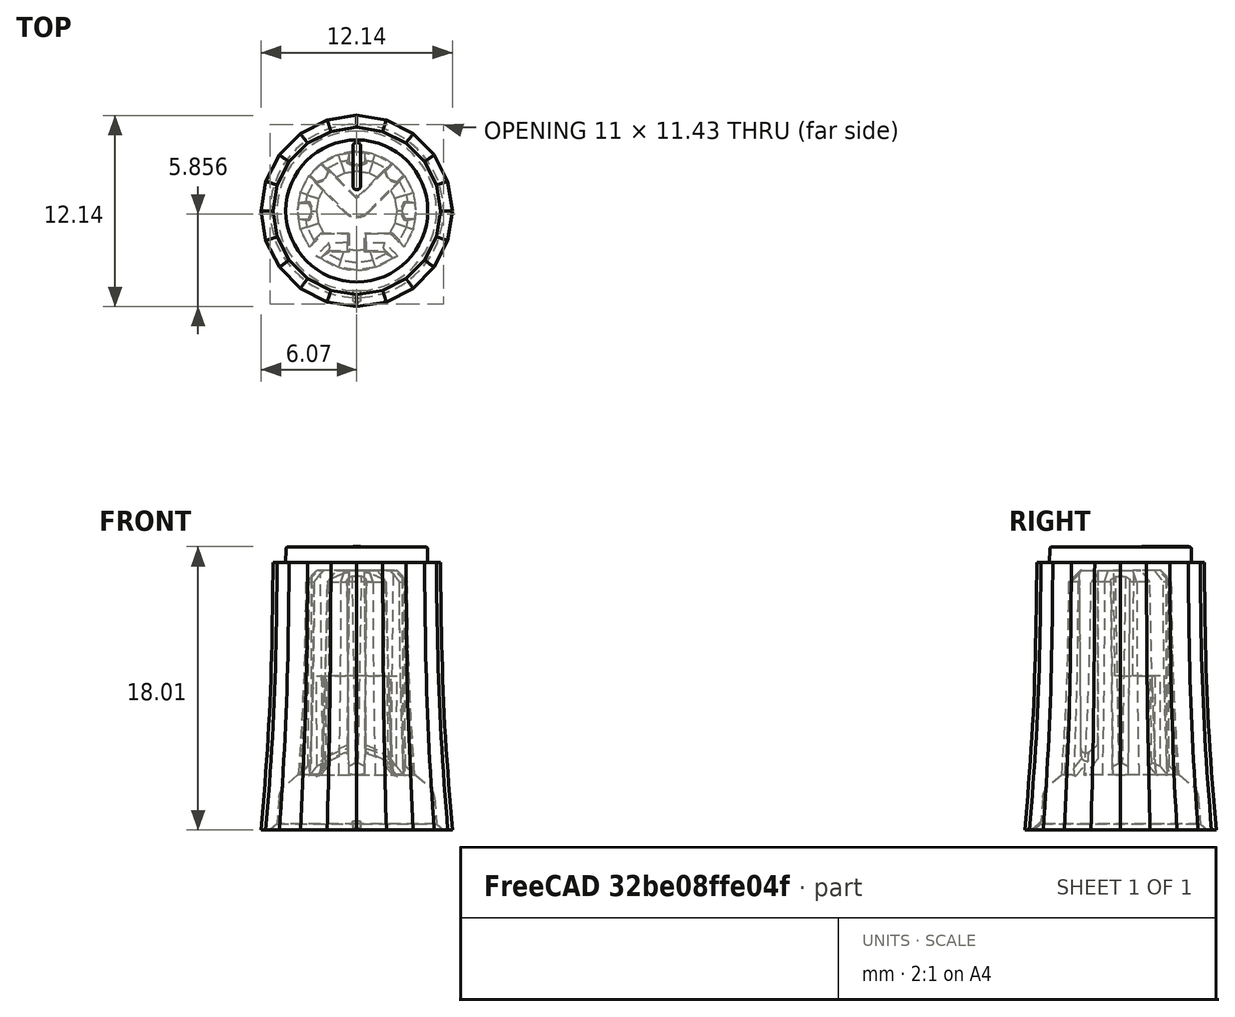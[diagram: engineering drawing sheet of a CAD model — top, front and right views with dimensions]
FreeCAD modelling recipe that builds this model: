
FCSTD DOCUMENT  (FreeCAD 0.21R33771 (Git))
Label: PLASTIC-KNOB-POT
License: All rights reserved
LicenseURL: https://en.wikipedia.org/wiki/All_rights_reserved
objects: TechDraw::DrawViewDimension×12, TechDraw::DrawHatch×11, TechDraw::DrawViewPart×9, TechDraw::DrawViewBalloon×7, Sketcher::SketchObject×3, TechDraw::DrawViewAnnotation×3, Part::Feature×2, PartDesign::Boolean×2, TechDraw::DrawSVGTemplate×2, PartDesign::Body×2, TechDraw::DrawPage×2, TechDraw::DrawComplexSection×1, PartDesign::Pad×1
note: 34 computed .brp shape members not serialized (recipe doc carries the construction recipe); baked Part::Feature solids carry a one-line shape summary decoded from their .brp

FEATURE [Part::Feature] Part__Feature  label="potmeter"
  shape: bbox 15.71 x 15.32 x 34.99 mm, 134 faces (baked)
FEATURE [PartDesign::Boolean] Boolean
  Group = -> [Part__Feature]
  Type = 0
FEATURE [TechDraw::DrawSVGTemplate] Template
  EditableTexts = COLOR=Black - RAL code: 9004; CreationDate=2024/01/02; E.G.APPROVED=APPROVED; FC-Scale=5:1; FC-Title=PLASTIC - KNOB - POT; IntechStudioLtd.=Intech Studio Ltd.; MATERIAL=ABS - Terluran GP22; REV=02; STANDARD=DIN 16742-TG4
  Height = 297
  Orientation = 1
  Template = <userpath>/Documents/grid-hardware/Manufacturing/FreeCAD_technical_drawing_template/A3_LandscapeTD_MODIFIED.svg
  Width = 420
FEATURE [Sketcher::SketchObject] Sketch
  FullyConstrained = true
  MapMode = 5
  Placement = pos=(0,0,0) rot=(1,0,0;1.5708rad)
  Support = -> [XZ_Plane]
  sketch-geometry (1):
    g0: LineSegment StartX=0 StartY=19 StartZ=0 EndX=0 EndY=-1 EndZ=0
  constraints (4):
    c: PointOnObject(g0,g-2)
    c: Vertical(g0)
    c: DistanceY(g0,g0) = 20
    c: DistanceY(g0,g-1) = 1
FEATURE [PartDesign::Body] Body  label="PLASTIC-KNOB-POT"
  Group = -> [Boolean,Sketch]
  Origin = -> Origin
  Tip = -> Boolean
FEATURE [TechDraw::DrawViewPart] View
  CoarseView = false
  Direction = (0,-1,0)
  Focus = 100
  HardHidden = false
  IsoCount = 0
  IsoHidden = false
  IsoVisible = true
  LockPosition = false
  Perspective = false
  Rotation = 0
  Scale = 5
  ScaleType = 2
  ScrubCount = 0
  SeamHidden = false
  SeamVisible = true
  SmoothHidden = false
  SmoothVisible = true
  Source = -> [Body]
  X = 98.421
  XDirection = (1,0,-1e-06)
  Y = 192.804
FEATURE [TechDraw::DrawViewPart] View001
  CoarseView = false
  Direction = (-1e-06,0,-1)
  Focus = 100
  HardHidden = false
  IsoCount = 0
  IsoHidden = false
  IsoVisible = true
  LockPosition = false
  Perspective = false
  Rotation = 0
  Scale = 5
  ScaleType = 2
  ScrubCount = 0
  SeamHidden = false
  SeamVisible = true
  SmoothHidden = false
  SmoothVisible = true
  Source = -> [Body]
  X = 305.681
  XDirection = (1,0,-1e-06)
  Y = 190.563
FEATURE [TechDraw::DrawComplexSection] ComplexSection  label="Section A - A"
  BaseView = -> View
  CoarseView = false
  CutSurfaceDisplay = 2
  CuttingToolWireObject = -> Sketch
  Direction = (-1,0,1e-06)
  FileGeomPattern = C:/Program Files/FreeCAD 0.21/data/Mod/TechDraw/PAT/FCPAT.pat
  FileHatchPattern = C:/Program Files/FreeCAD 0.21/data/Mod/TechDraw/Patterns/simple.svg
  Focus = 100
  FuseBeforeCut = false
  HardHidden = false
  HatchOffset = (0,0,0)
  HatchRotation = 0
  HatchScale = 1
  IsoCount = 0
  IsoHidden = false
  IsoVisible = false
  LockPosition = false
  NameGeomPattern = Gyémánt bevonatú
  Perspective = false
  ProjectionStrategy = 0
  Rotation = -90
  Scale = 5
  ScaleType = 2
  ScrubCount = 0
  SeamHidden = false
  SeamVisible = true
  SectionDirection = 4
  SectionNormal = (-1,0,1e-06)
  SectionOrigin = (0,0,0)
  SectionSymbol = A
  SmoothHidden = false
  SmoothVisible = true
  Source = -> [Body]
  TrimAfterCut = false
  X = 193.37
  XDirection = (-1e-06,0,-1)
  Y = 193.697
FEATURE [TechDraw::DrawHatch] Hatch  label="HatchF1"
  HatchPattern = C:/Program Files/FreeCAD 0.21/data/Mod/TechDraw/Patterns/simple.svg
  Source = -> ComplexSection [Face1]
FEATURE [TechDraw::DrawViewDimension] Dimension
  AngleOverride = false
  Arbitrary = false
  ArbitraryTolerances = false
  EqualTolerance = true
  ExtensionAngle = 0
  FormatSpec = %.2w
  FormatSpecOverTolerance = %+.2w
  FormatSpecUnderTolerance = %+.2w
  Inverted = false
  LineAngle = 0
  LockPosition = false
  MeasureType = 1
  OverTolerance = 0.1
  References2D = -> [ComplexSection]
  Rotation = 0
  ScaleType = 0
  TheoreticalExact = false
  Type = 2
  UnderTolerance = -0.1
  X = 46.2416
  Y = -17.976
FEATURE [TechDraw::DrawViewDimension] Dimension001
  AngleOverride = false
  Arbitrary = false
  ArbitraryTolerances = false
  EqualTolerance = false
  ExtensionAngle = 0
  FormatSpec = ⌀%.1w
  FormatSpecOverTolerance = %+.2w
  FormatSpecUnderTolerance = %+.2w
  Inverted = false
  LineAngle = 0
  LockPosition = false
  MeasureType = 1
  OverTolerance = 0.1
  References2D = -> [ComplexSection]
  Rotation = 0
  ScaleType = 0
  TheoreticalExact = false
  Type = 1
  UnderTolerance = 0
  X = 45.3884
  Y = -50.1957
FEATURE [TechDraw::DrawViewDimension] Dimension003
  AngleOverride = false
  Arbitrary = false
  ArbitraryTolerances = false
  EqualTolerance = true
  ExtensionAngle = 0
  FormatSpec = %.2w
  FormatSpecOverTolerance = %+.2w
  FormatSpecUnderTolerance = %+.2w
  Inverted = false
  LineAngle = 0
  LockPosition = false
  MeasureType = 1
  OverTolerance = 0
  References2D = -> [View]
  Rotation = 0
  ScaleType = 0
  TheoreticalExact = false
  Type = 2
  UnderTolerance = 0
  X = -57.7221
  Y = 0.521046
FEATURE [TechDraw::DrawViewDimension] Dimension004
  AngleOverride = false
  Arbitrary = false
  ArbitraryTolerances = false
  EqualTolerance = true
  ExtensionAngle = 0
  FormatSpec = %.2w
  FormatSpecOverTolerance = %+.2w
  FormatSpecUnderTolerance = %+.2w
  Inverted = false
  LineAngle = 0
  LockPosition = false
  MeasureType = 1
  OverTolerance = 0
  References2D = -> [View]
  Rotation = 0
  ScaleType = 0
  TheoreticalExact = false
  Type = 2
  UnderTolerance = 0
  X = 39.126
  Y = 37.6793
FEATURE [TechDraw::DrawViewDimension] Dimension005
  AngleOverride = false
  Arbitrary = false
  ArbitraryTolerances = false
  EqualTolerance = true
  ExtensionAngle = 0
  FormatSpec = ⌀%.2w
  FormatSpecOverTolerance = %+.2w
  FormatSpecUnderTolerance = %+.2w
  Inverted = false
  LineAngle = 0
  LockPosition = false
  MeasureType = 1
  OverTolerance = 0
  References2D = -> [View001]
  Rotation = 0
  ScaleType = 0
  TheoreticalExact = false
  Type = 5
  UnderTolerance = 0
  X = -41.2084
  Y = 24.1058
FEATURE [TechDraw::DrawViewDimension] Dimension006
  AngleOverride = false
  Arbitrary = true
  ArbitraryTolerances = false
  EqualTolerance = true
  ExtensionAngle = 0
  FormatSpec = 5,797±0,05
  FormatSpecOverTolerance = %+.2w
  FormatSpecUnderTolerance = %+.2w
  Inverted = false
  LineAngle = 0
  LockPosition = false
  MeasureType = 1
  OverTolerance = 0.05
  References2D = -> [View001]
  Rotation = 0
  ScaleType = 0
  TheoreticalExact = false
  Type = 1
  UnderTolerance = -0.05
  X = -0.153255
  Y = 40.8913
FEATURE [TechDraw::DrawViewDimension] Dimension007
  AngleOverride = false
  Arbitrary = false
  ArbitraryTolerances = false
  EqualTolerance = true
  ExtensionAngle = 0
  FormatSpec = %.2w
  FormatSpecOverTolerance = %+.2w
  FormatSpecUnderTolerance = %+.2w
  Inverted = false
  LineAngle = 0
  LockPosition = false
  MeasureType = 1
  OverTolerance = 0.05
  References2D = -> [View001]
  Rotation = 0
  ScaleType = 0
  TheoreticalExact = false
  Type = 2
  UnderTolerance = -0.05
  X = 40.9222
  Y = 25.266
FEATURE [TechDraw::DrawViewDimension] Dimension008
  AngleOverride = false
  Arbitrary = false
  ArbitraryTolerances = false
  EqualTolerance = true
  ExtensionAngle = 0
  FormatSpec = ⌀%.0w
  FormatSpecOverTolerance = %+.2w
  FormatSpecUnderTolerance = %+.2w
  Inverted = false
  LineAngle = 0
  LockPosition = false
  MeasureType = 1
  OverTolerance = 0
  References2D = -> [View]
  Rotation = 0
  ScaleType = 0
  TheoreticalExact = false
  Type = 1
  UnderTolerance = 0
  X = -8.5e-05
  Y = 63.706
FEATURE [TechDraw::DrawViewPart] View003
  CoarseView = false
  Direction = (-0.57735,-0.57735,0.57735)
  Focus = 100
  HardHidden = false
  IsoCount = 0
  IsoHidden = false
  IsoVisible = true
  LockPosition = false
  Perspective = false
  Rotation = 0
  Scale = 2
  ScaleType = 2
  ScrubCount = 0
  SeamHidden = false
  SeamVisible = true
  SmoothHidden = false
  SmoothVisible = true
  Source = -> [Body]
  X = 379.046
  XDirection = (0.707107,-0.707107,0)
  Y = 107.401
FEATURE [TechDraw::DrawViewPart] View004
  CoarseView = false
  Direction = (-0.57735,-0.57735,-0.57735)
  Focus = 100
  HardHidden = false
  IsoCount = 0
  IsoHidden = false
  IsoVisible = true
  LockPosition = false
  Perspective = false
  Rotation = 0
  Scale = 2
  ScaleType = 2
  ScrubCount = 0
  SeamHidden = false
  SeamVisible = true
  SmoothHidden = false
  SmoothVisible = true
  Source = -> [Body]
  X = 343.996
  XDirection = (0.707106,-0.707106,0)
  Y = 107.801
FEATURE [TechDraw::DrawHatch] Hatch001  label="Hatch001F2"
  HatchPattern = C:/Program Files/FreeCAD 0.21/data/Mod/TechDraw/Patterns/solid.svg
  Source = -> View003 [Face2,Face13,Face4,Face5,Face3,Face6,Face9,Face8,Face7,Face12,Face11,Face10]
FEATURE [TechDraw::DrawHatch] Hatch002  label="Hatch002F1"
  HatchPattern = C:/Program Files/FreeCAD 0.21/data/Mod/TechDraw/Patterns/solid.svg
  Source = -> View003 [Face1]
FEATURE [TechDraw::DrawHatch] Hatch003  label="Hatch003F19"
  HatchPattern = C:/Program Files/FreeCAD 0.21/data/Mod/TechDraw/Patterns/solid.svg
  Source = -> View004 [Face19,Face8,Face4,Face7,Face3,Face5,Face6,Face9,Face13,Face14]
FEATURE [TechDraw::DrawHatch] Hatch004  label="Hatch004F16"
  HatchPattern = C:/Program Files/FreeCAD 0.21/data/Mod/TechDraw/Patterns/solid.svg
  Source = -> View004 [Face16,Face22,Face23,Face11,Face18,Face21]
FEATURE [TechDraw::DrawHatch] Hatch005  label="Hatch005F15"
  HatchPattern = C:/Program Files/FreeCAD 0.21/data/Mod/TechDraw/Patterns/solid.svg
  Source = -> View004 [Face15,Face20,Face17,Face10,Face1,Face12]
FEATURE [TechDraw::DrawHatch] Hatch006  label="Hatch006F32"
  HatchPattern = C:/Program Files/FreeCAD 0.21/data/Mod/TechDraw/Patterns/solid.svg
  Source = -> View004 [Face32,Face31,Face24,Face25,Face27,Face28,Face29,Face30,Face33]
FEATURE [TechDraw::DrawHatch] Hatch007  label="Hatch007F34"
  HatchPattern = C:/Program Files/FreeCAD 0.21/data/Mod/TechDraw/Patterns/solid.svg
  Source = -> View004 [Face34]
FEATURE [TechDraw::DrawSVGTemplate] Template001
  EditableTexts = COLOR=White - RAL code: 9003; CreationDate=2024/01/02; E.G.APPROVED=APPROVED; FC-Scale=5:1; FC-Title=Potmeter knob painting; IntechStudioLtd.=Intech Studio Ltd.; MATERIAL=Tampo or screen printing; REV=02; STANDARD=N/A
  Height = 297
  Orientation = 1
  Template = <userpath>/Documents/grid-hardware/Manufacturing/FreeCAD_technical_drawing_template/A3_LandscapeTD_MODIFIED.svg
  Width = 420
FEATURE [TechDraw::DrawViewAnnotation] Annotation
  Font = osifont
  LineSpace = 100
  LockPosition = false
  MaxWidth = -1
  Rotation = 0
  ScaleType = 0
  Text = Painting material: | Resistance against scratches is critical to quality | Color: White - RAL code: 9003
  TextSize = 4
  TextStyle = 0
  X = 275.791
  Y = 85.9122
FEATURE [Part::Feature] Part__Feature001  label="potmeter001"
  shape: bbox 15.71 x 15.32 x 34.99 mm, 134 faces (baked)
FEATURE [PartDesign::Boolean] Boolean001
  Group = -> [Part__Feature001]
  Type = 0
FEATURE [Sketcher::SketchObject] Sketch002
  FullyConstrained = true
  MapMode = 5
  Placement = pos=(0,0,0) rot=(1,0,0;1.5708rad)
  Support = -> [XZ_Plane001]
  sketch-geometry (1):
    g0: LineSegment StartX=0 StartY=19 StartZ=0 EndX=0 EndY=-1 EndZ=0
  constraints (4):
    c: PointOnObject(g0,g-2)
    c: Vertical(g0)
    c: DistanceY(g0,g0) = 20
    c: DistanceY(g0,g-1) = 1
FEATURE [Sketcher::SketchObject] Sketch003
  ExternalGeometry = -> [Boolean001]
  FullyConstrained = true
  MapMode = 5
  Placement = pos=(0,0,18) rot=(0,0,1;0rad)
  Support = -> [Boolean001]
  sketch-geometry (5):
    g0: ArcOfCircle CenterX=0 CenterY=1.6013 CenterZ=0 NormalX=0 NormalY=0 NormalZ=1 AngleXU=0 Radius=0.25 StartAngle=3.14159 EndAngle=6.28319
    g1: ArcOfCircle CenterX=0 CenterY=4.1013 CenterZ=0 NormalX=0 NormalY=0 NormalZ=1 AngleXU=0 Radius=0.25 StartAngle=1.728e-12 EndAngle=3.14159
    g2: LineSegment StartX=0 StartY=4.3513 StartZ=0 EndX=0 EndY=1.3513 EndZ=0
    g3: LineSegment StartX=-0.25 StartY=4.1013 StartZ=0 EndX=-0.25 EndY=1.6013 EndZ=0
    g4: LineSegment StartX=0.25 StartY=4.1013 StartZ=0 EndX=0.25 EndY=1.6013 EndZ=0
  constraints (14):
    c: PointOnObject(g0,g-2)
    c: PointOnObject(g1,g-2)
    c: Tangent(g1,g-3)
    c: PointOnObject(g2,g1)
    c: PointOnObject(g2,g0)
    c: Vertical(g2)
    c: Equal(g0,g1)
    c: Diameter(g1) = 0.5
    c: PointOnObject(g2,g-2)
    c: Tangent(g1,g4) = 1.5708
    c: Tangent(g1,g3) = -1.5708
    c: Tangent(g0,g3) = -1.5708
    c: Tangent(g0,g4) = 1.5708
    c: DistanceY(g2,g2) = 3
FEATURE [PartDesign::Pad] Pad  label="Paint"
  BaseFeature = -> Boolean001
  Direction = (0,0,1)
  Length = 0.01
  Length2 = 10
  Profile = -> Sketch003
  ReferenceAxis = -> Sketch003 [N_Axis]
  Type = 0
FEATURE [PartDesign::Body] Body001  label="PLASTIC-KNOB_Painted"
  Group = -> [Boolean001,Sketch002,Sketch003,Pad]
  Origin = -> Origin001
  Tip = -> Pad
FEATURE [TechDraw::DrawViewPart] View005
  CoarseView = false
  Direction = (0,0,1)
  Focus = 100
  HardHidden = false
  IsoCount = 0
  IsoHidden = false
  IsoVisible = true
  LockPosition = false
  Perspective = false
  Rotation = 0
  Scale = 5
  ScaleType = 2
  ScrubCount = 0
  SeamHidden = false
  SeamVisible = true
  SmoothHidden = false
  SmoothVisible = true
  Source = -> [Pad]
  X = 97.3884
  XDirection = (1,0,0)
  Y = 204.513
FEATURE [TechDraw::DrawViewPart] View006
  CoarseView = false
  Direction = (-1,0,0)
  Focus = 100
  HardHidden = false
  IsoCount = 0
  IsoHidden = false
  IsoVisible = true
  LockPosition = false
  Perspective = false
  Rotation = 0
  Scale = 5
  ScaleType = 2
  ScrubCount = 0
  SeamHidden = false
  SeamVisible = true
  SmoothHidden = false
  SmoothVisible = true
  Source = -> [Pad]
  X = 207.371
  XDirection = (0,0,1)
  Y = 204.153
FEATURE [TechDraw::DrawViewPart] View007
  CoarseView = false
  Direction = (0.57735,0.57735,0.57735)
  Focus = 100
  HardHidden = false
  IsoCount = 0
  IsoHidden = false
  IsoVisible = true
  LockPosition = false
  Perspective = false
  Rotation = 0
  Scale = 5
  ScaleType = 2
  ScrubCount = 0
  SeamHidden = false
  SeamVisible = true
  SmoothHidden = false
  SmoothVisible = true
  Source = -> [Pad]
  X = 121.95
  XDirection = (-0.707107,0.707107,5.7735e-07)
  Y = 74.2227
FEATURE [TechDraw::DrawViewPart] View008
  CoarseView = false
  Direction = (0,0,-1)
  Focus = 100
  HardHidden = false
  IsoCount = 0
  IsoHidden = false
  IsoVisible = true
  LockPosition = false
  Perspective = false
  Rotation = 0
  Scale = 5
  ScaleType = 2
  ScrubCount = 0
  SeamHidden = false
  SeamVisible = true
  SmoothHidden = false
  SmoothVisible = true
  Source = -> [Pad]
  X = 327.125
  XDirection = (-1,0,0)
  Y = 202.189
FEATURE [TechDraw::DrawHatch] Hatch008  label="Hatch008F6"
  HatchPattern = C:/Program Files/FreeCAD 0.21/data/Mod/TechDraw/Patterns/solid.svg
  Source = -> View005 [Face6]
FEATURE [TechDraw::DrawViewDimension] Dimension010
  AngleOverride = false
  Arbitrary = false
  ArbitraryTolerances = false
  EqualTolerance = true
  ExtensionAngle = 0
  FormatSpec = %.2w
  FormatSpecOverTolerance = %+.2w
  FormatSpecUnderTolerance = %+.2w
  Inverted = false
  LineAngle = 0
  LockPosition = false
  MeasureType = 1
  OverTolerance = 0
  References2D = -> [View005]
  Rotation = 0
  ScaleType = 0
  TheoreticalExact = false
  Type = 2
  UnderTolerance = 0
  X = -41.9183
  Y = 15.656
FEATURE [TechDraw::DrawViewDimension] Dimension011
  AngleOverride = false
  Arbitrary = false
  ArbitraryTolerances = false
  EqualTolerance = true
  ExtensionAngle = 0
  FormatSpec = %.2w
  FormatSpecOverTolerance = %+.2w
  FormatSpecUnderTolerance = %+.2w
  Inverted = false
  LineAngle = 0
  LockPosition = false
  MeasureType = 1
  OverTolerance = 0
  References2D = -> [View005]
  Rotation = 0
  ScaleType = 0
  TheoreticalExact = false
  Type = 1
  UnderTolerance = 0
  X = 34.5367
  Y = 20.8774
FEATURE [TechDraw::DrawHatch] Hatch009  label="Hatch009F17"
  HatchPattern = C:/Program Files/FreeCAD 0.21/data/Mod/TechDraw/Patterns/solid.svg
  Source = -> View007 [Face17,Face18,Face12,Face8,Face7,Face4,Face3,Face5,Face6,Face9,Face11,Face10,Face13,Face14,Face1]
FEATURE [TechDraw::DrawHatch] Hatch010  label="Hatch010F2"
  HatchPattern = C:/Program Files/FreeCAD 0.21/data/Mod/TechDraw/Patterns/solid.svg
  Source = -> View007 [Face2]
FEATURE [TechDraw::DrawViewBalloon] Balloon002
  BubbleShape = 1
  EndType = 0
  EndTypeScale = 1
  KinkLength = 0.1
  LockPosition = false
  OriginX = -4.24264
  OriginY = -4.24264
  Rotation = 0
  ScaleType = 0
  ShapeScale = 1
  SourceView = -> View008
  TextWrapLen = -1
  X = -5.3055
  Y = -10.5429
FEATURE [TechDraw::DrawViewAnnotation] Annotation001
  Font = osifont
  LineSpace = 100
  LockPosition = false
  MaxWidth = -1
  Rotation = 0
  ScaleType = 0
  Text = AESTHETICAL SURFACES: | COLORED BLUE ON THE ISOMETRIC VIEWS: SPI - D2 | NO BURRS, NO PARTING LINES, | NO EJECTION MARKS | FREE OF ANY DEFECTS | FREE OF ANY WELD OR MELD LINES | NON VISIBLE GATE LOCATION ALLOWED | REMAINING BLACK SURFACES: SPI - B2
  TextSize = 3
  TextStyle = 0
  X = 264.167
  Y = 100.12
FEATURE [TechDraw::DrawViewBalloon] Balloon
  BubbleShape = 1
  EndType = 3
  EndTypeScale = 1
  KinkLength = 0
  LockPosition = false
  OriginX = -2.29422
  OriginY = 3.04373
  Rotation = 0
  ScaleType = 0
  ShapeScale = 1
  SourceView = -> View004
  TextWrapLen = -1
  X = -16.2526
  Y = -5.35905
FEATURE [TechDraw::DrawViewPart] View002
  CoarseView = false
  Direction = (1e-06,0,1)
  Focus = 100
  HardHidden = false
  IsoCount = 0
  IsoHidden = false
  IsoVisible = true
  LockPosition = false
  Perspective = false
  Rotation = 0
  Scale = 5
  ScaleType = 2
  ScrubCount = 0
  SeamHidden = false
  SeamVisible = true
  SmoothHidden = false
  SmoothVisible = true
  Source = -> [Body]
  X = 100.462
  XDirection = (1,0,-1e-06)
  Y = 74.8021
FEATURE [TechDraw::DrawViewDimension] Dimension009
  AngleOverride = false
  Arbitrary = false
  ArbitraryTolerances = false
  EqualTolerance = true
  ExtensionAngle = 0
  FormatSpec = 10× %.2w
  FormatSpecOverTolerance = %+.2w
  FormatSpecUnderTolerance = %+.2w
  Inverted = false
  LineAngle = 0
  LockPosition = false
  MeasureType = 1
  OverTolerance = 0
  References2D = -> [View002]
  Rotation = 0
  ScaleType = 0
  TheoreticalExact = false
  Type = 0
  UnderTolerance = 0
  X = -39.2324
  Y = 9.93901
FEATURE [TechDraw::DrawViewDimension] Dimension012
  AngleOverride = false
  Arbitrary = false
  ArbitraryTolerances = false
  EqualTolerance = true
  ExtensionAngle = 0
  FormatSpec = (%.2w)
  FormatSpecOverTolerance = %+.2w
  FormatSpecUnderTolerance = %+.2w
  Inverted = false
  LineAngle = 0
  LockPosition = false
  MeasureType = 1
  OverTolerance = 0
  References2D = -> [View005]
  Rotation = 0
  ScaleType = 0
  TheoreticalExact = false
  Type = 2
  UnderTolerance = 0
  X = -37.4834
  Y = -5.49655
FEATURE [TechDraw::DrawViewBalloon] Balloon003
  BubbleShape = 1
  EndType = 0
  EndTypeScale = 1
  KinkLength = -0.1
  LockPosition = false
  OriginX = 1.59e-14
  OriginY = 1.3513
  Rotation = 0
  ScaleType = 0
  ShapeScale = 1
  SourceView = -> View005
  Text = Orientation of the painted line relative to inner geometry is critical to quality
  TextWrapLen = -1
  X = 24.0964
  Y = -11.4876
FEATURE [TechDraw::DrawViewBalloon] Balloon004
  BubbleShape = 2
  EndType = 6
  EndTypeScale = 1
  KinkLength = 0
  LockPosition = false
  OriginX = -50.6224
  OriginY = 14.8162
  Rotation = 0
  ScaleType = 0
  ShapeScale = 1
  SourceView = -> Dimension010
  Text = 2
  TextWrapLen = -1
  X = -51.7505
  Y = 12.4076
FEATURE [TechDraw::DrawViewBalloon] Balloon005
  BubbleShape = 2
  EndType = 0
  EndTypeScale = 1
  KinkLength = 0
  LockPosition = false
  OriginX = 35.0518
  OriginY = 20.0598
  Rotation = 0
  ScaleType = 0
  ShapeScale = 1
  SourceView = -> Dimension011
  Text = 2
  TextWrapLen = -1
  X = 45.9782
  Y = 13.5369
FEATURE [TechDraw::DrawPage] Page001  label="PLASTIC-KNOB-POT_Painting drawing"
  KeepUpdated = true
  NextBalloonIndex = 9
  ProjectionType = 0
  Template = -> Template001
  Views = -> [Annotation,View005,View006,View007,View008,Dimension010,Dimension011,Balloon002,Dimension012,Balloon003,Balloon004,Balloon005]
FEATURE [TechDraw::DrawViewBalloon] Balloon006
  BubbleShape = 2
  EndType = 6
  EndTypeScale = 1
  KinkLength = 0
  LockPosition = false
  OriginX = -56.8835
  OriginY = 6.88697
  Rotation = 0
  ScaleType = 0
  ShapeScale = 1
  SourceView = -> Annotation001
  Text = 2
  TextWrapLen = -1
  X = 52.947
  Y = 15.281
FEATURE [TechDraw::DrawViewBalloon] Balloon007
  BubbleShape = 2
  EndType = 6
  EndTypeScale = 1
  KinkLength = 0
  LockPosition = false
  OriginX = -68.2573
  OriginY = 1.31609
  Rotation = 0
  ScaleType = 0
  ShapeScale = 1
  SourceView = -> Annotation001
  Text = 2
  TextWrapLen = -1
  X = 30.6635
  Y = -9.09163
FEATURE [TechDraw::DrawViewAnnotation] Annotation002
  Font = osifont
  LineSpace = 100
  LockPosition = false
  MaxWidth = -1
  Rotation = 0
  ScaleType = 0
  Text = Section A-A
  TextSize = 4
  TextStyle = 0
  X = 194.876
  Y = 128.632
FEATURE [TechDraw::DrawPage] Page  label="PLASTIC-KNOB-POT_Drawing"
  KeepUpdated = true
  NextBalloonIndex = 5
  ProjectionType = 0
  Template = -> Template
  Views = -> [View,View001,View002,ComplexSection,Dimension,Dimension001,Dimension003,Dimension004,Dimension005,Dimension006,Dimension007,Dimension008,Dimension009,View003,View004,Annotation001,Balloon,Balloon006,Balloon007,Annotation002]
